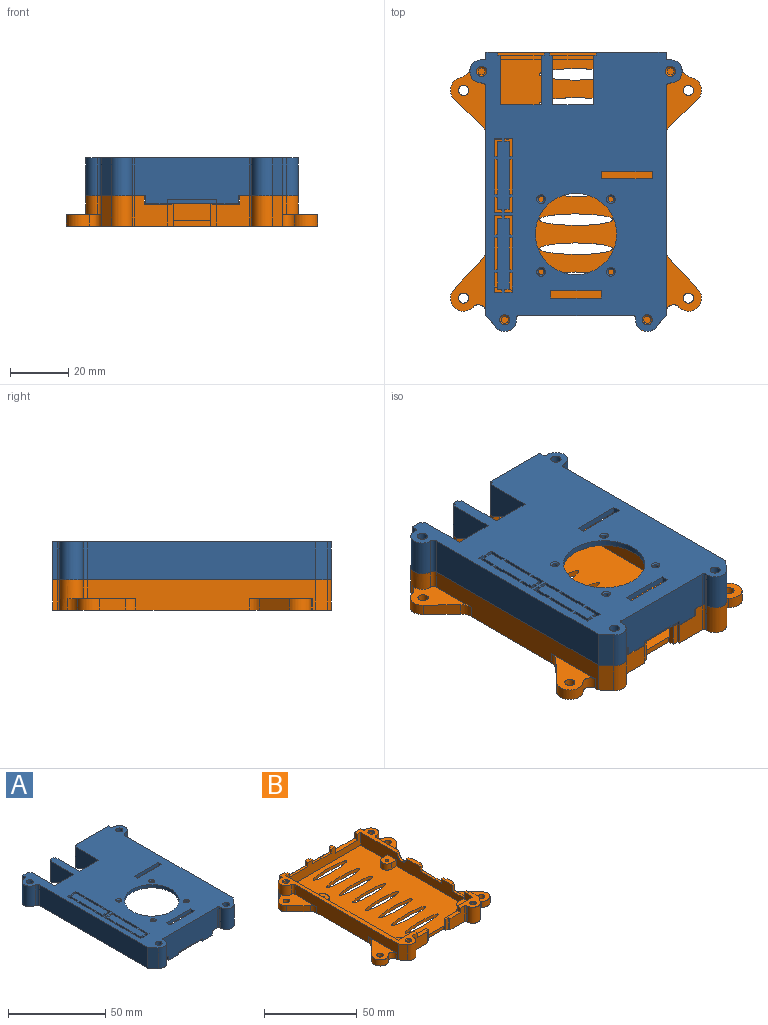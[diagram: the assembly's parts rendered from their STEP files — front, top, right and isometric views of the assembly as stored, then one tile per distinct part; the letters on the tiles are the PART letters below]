
ASSEMBLY  parts=2 mates=1
PART A: 159 faces, bbox 73x96x15.8 mm
  f0: plane 32x2.5mm, normal (0,0,-1), area 63mm2, adj f67,f68,f153,f154,f155,f156,f157
  f1: plane 96x20.5mm, normal (0,0,-1), area 322.4mm2, adj f67,f68,f69,f70,f71,f72,f73,f74
  f2: plane 30.5x10.5mm, normal (0,0,-1), area 109.1mm2, adj f3,f4,f65,f90,f91,f92,f93,f94
  f3: plane 78.5x13mm, normal (1,0,0), area 841.2mm2, adj f2,f5,f6,f52,f85,f89,f90,f140
  f4: plane 85.5x11mm, normal (-1,0,0), area 848.3mm2, adj f2,f5,f6,f7,f68,f85,f96,f136
  f5: plane 10.5x2.5mm, normal (0,0,-1), area 22.8mm2, adj f3,f4,f144,f146,f147,f150,f151,f152
  f6: plane 8.5x2.5mm, normal (0,0,-1), area 17.8mm2, adj f3,f4,f137,f139,f140,f143,f146,f148
  f7: plane 85.5x57mm, normal (0,0,-1), area 2695.7mm2, adj f4,f53,f59,f63,f64,f68,f69,f70
  f8: plane 12x1.2mm, normal (1,0,0), area 14.4mm2, adj f9,f10,f52,f134
  f9: plane 1.2x1mm, normal (0,-1,0), area 1.2mm2, adj f8,f52,f125,f134
  f10: plane 1.2x1mm, normal (0,1,0), area 1.2mm2, adj f8,f52,f125,f134
  f11: plane 1.2x1mm, normal (0,-1,0), area 1.2mm2, adj f13,f52,f123,f134
  f12: plane 1.2x1mm, normal (0,1,0), area 1.2mm2, adj f13,f52,f123,f134
  f13: plane 12x1.2mm, normal (-1,0,0), area 14.4mm2, adj f11,f12,f52,f134
  f14: plane 1.2x1mm, normal (-1,0,0), area 1.2mm2, adj f16,f52,f106,f134
  f15: plane 1.2x1mm, normal (0,-1,0), area 1.2mm2, adj f17,f52,f123,f134
  f16: plane 1.5x1.2mm, normal (0,-1,0), area 1.8mm2, adj f14,f17,f52,f134
  f17: plane 4.25x1.2mm, normal (-1,0,0), area 5.1mm2, adj f15,f16,f52,f134
  f18: plane 1.2x1mm, normal (0,-1,0), area 1.2mm2, adj f20,f52,f125,f134
  f19: plane 1.2x1mm, normal (1,0,0), area 1.2mm2, adj f21,f52,f106,f134
  f20: plane 4.25x1.2mm, normal (1,0,0), area 5.1mm2, adj f18,f21,f52,f134
  f21: plane 1.5x1.2mm, normal (0,-1,0), area 1.8mm2, adj f19,f20,f52,f134
  f22: plane 1.2x1mm, normal (1,0,0), area 1.2mm2, adj f23,f52,f107,f135
  f23: plane 1.5x1.2mm, normal (0,1,0), area 1.8mm2, adj f22,f24,f52,f135
  f24: plane 5.75x1.2mm, normal (1,0,0), area 6.9mm2, adj f23,f25,f52,f135
  f25: plane 1.2x1mm, normal (0,1,0), area 1.2mm2, adj f24,f52,f122,f135
  f26: plane 1.2x1mm, normal (0,1,0), area 1.2mm2, adj f27,f52,f120,f135
  f27: plane 5.75x1.2mm, normal (-1,0,0), area 6.9mm2, adj f26,f28,f52,f135
  f28: plane 1.5x1.2mm, normal (0,1,0), area 1.8mm2, adj f27,f29,f52,f135
  f29: plane 1.2x1mm, normal (-1,0,0), area 1.2mm2, adj f28,f52,f107,f135
  f30: plane 1.2x1mm, normal (0,-1,0), area 1.2mm2, adj f32,f52,f120,f135
  f31: plane 1.2x1mm, normal (0,1,0), area 1.2mm2, adj f32,f52,f120,f135
  f32: plane 11x1.2mm, normal (-1,0,0), area 13.2mm2, adj f30,f31,f52,f135
  f33: plane 1.2x1mm, normal (0,-1,0), area 1.2mm2, adj f34,f52,f122,f135
  f34: plane 11x1.2mm, normal (1,0,0), area 13.2mm2, adj f33,f35,f52,f135
  f35: plane 1.2x1mm, normal (0,1,0), area 1.2mm2, adj f34,f52,f122,f135
  f36: plane 1.2x1mm, normal (-1,0,0), area 1.2mm2, adj f37,f52,f121,f135
  f37: plane 1.5x1.2mm, normal (0,-1,0), area 1.8mm2, adj f36,f38,f52,f135
  f38: plane 5.75x1.2mm, normal (-1,0,0), area 6.9mm2, adj f37,f39,f52,f135
  f39: plane 1.2x1mm, normal (0,-1,0), area 1.2mm2, adj f38,f52,f120,f135
  f40: plane 1.2x1mm, normal (0,-1,0), area 1.2mm2, adj f42,f52,f122,f135
  f41: plane 1.2x1mm, normal (1,0,0), area 1.2mm2, adj f43,f52,f121,f135
  f42: plane 5.75x1.2mm, normal (1,0,0), area 6.9mm2, adj f40,f43,f52,f135
  f43: plane 1.5x1.2mm, normal (0,-1,0), area 1.8mm2, adj f41,f42,f52,f135
  f44: plane 1.2x1mm, normal (0,1,0), area 1.2mm2, adj f45,f52,f123,f134
  f45: plane 5.25x1.2mm, normal (-1,0,0), area 6.3mm2, adj f44,f46,f52,f134
  f46: plane 1.5x1.2mm, normal (0,1,0), area 1.8mm2, adj f45,f47,f52,f134
  f47: plane 1.2x1mm, normal (-1,0,0), area 1.2mm2, adj f46,f52,f124,f134
  f48: plane 1.2x1mm, normal (1,0,0), area 1.2mm2, adj f49,f52,f124,f134
  f49: plane 1.5x1.2mm, normal (0,1,0), area 1.8mm2, adj f48,f50,f52,f134
  f50: plane 5.25x1.2mm, normal (1,0,0), area 6.3mm2, adj f49,f51,f52,f134
  f51: plane 1.2x1mm, normal (0,1,0), area 1.2mm2, adj f50,f52,f125,f134
  f52: plane 96x73mm, normal (0,0,1), area 4382.9mm2, adj f3,f8,f9,f10,f11,f12,f13,f14
  f53: plane 32x13mm, normal (1,0,0), area 186.2mm2, adj f7,f52,f54,f60,f97,f99,f103,f104
  f54: plane 13x1mm, normal (0,1,0), area 13mm2, adj f52,f53,f55,f60
  f55: plane 13x1mm, normal (1,0,0), area 13mm2, adj f52,f54,f56,f60
  f56: plane 13x2mm, normal (0,1,0), area 26mm2, adj f52,f55,f57,f60
  f57: plane 13x1mm, normal (-1,0,0), area 13mm2, adj f52,f56,f58,f60
  f58: plane 13x1mm, normal (0,1,0), area 13mm2, adj f52,f57,f59,f60
  f59: plane 24x13mm, normal (-1,0,0), area 174.3mm2, adj f7,f52,f58,f60,f98,f99
  f60: plane 4x2.5mm, normal (0,0,-1), area 8mm2, adj f53,f54,f55,f56,f57,f58,f59,f99
  f61: plane 13x1mm, normal (-1,0,0), area 13mm2, adj f52,f62,f65,f66
  f62: plane 13x1mm, normal (0,1,0), area 13mm2, adj f52,f61,f63,f66
  f63: plane 32x13mm, normal (-1,0,0), area 186.3mm2, adj f7,f52,f62,f66,f97,f100,f103,f104
  f64: plane 25x11.8mm, normal (1,0,0), area 169.6mm2, adj f7,f65,f66,f100,f101,f102
  f65: plane 24x13mm, normal (0,1,0), area 111.4mm2, adj f2,f52,f61,f64,f66,f94,f95,f102
  f66: plane 3x2.5mm, normal (0,0,-1), area 6.5mm2, adj f61,f62,f63,f64,f65,f100
  f67: plane 39.5x15.8mm, normal (0,-1,0), area 577.6mm2, adj f0,f1,f52,f84,f85,f86,f153,f154
  f68: plane 57x13.8mm, normal (0,1,0), area 716.6mm2, adj f0,f1,f4,f7,f69,f85,f153,f154
  f69: plane 85.5x11mm, normal (1,0,0), area 940.5mm2, adj f1,f7,f68,f70
  f70: plane 11x2.5mm, normal (0,-1,0), area 27.5mm2, adj f1,f7,f69,f71
  f71: plane 17x13mm, normal (1,0,0), area 50.5mm2, adj f1,f7,f52,f70,f72,f98
  f72: plane 13x1mm, normal (0,1,0), area 13mm2, adj f1,f52,f71,f73
  f73: plane 13x1mm, normal (1,0,0), area 13mm2, adj f1,f52,f72,f74
  f74: plane 13x4mm, normal (0,1,0), area 52mm2, adj f1,f52,f73,f75
  f75: plane 13x1.75mm, normal (-1,0,0), area 22.8mm2, adj f1,f52,f74,f76
  f76: cylinder r=0.75mm len=13mm, axis (0,0,-1), area 15.3mm2, adj f1,f52,f75,f77
  f77: plane 13x0.75mm, normal (0,1,0), area 9.7mm2, adj f1,f52,f76,f78
  f78: cylinder r=4mm len=13mm, axis (0,0,-1), area 163.4mm2, adj f1,f52,f77,f79
  f79: cylinder r=1.5mm len=13mm, axis (0,0,-1), area 30.6mm2, adj f1,f52,f78,f80
  f80: plane 78.5x13mm, normal (-1,0,0), area 1020.5mm2, adj f1,f52,f79,f81
  f81: plane 13x4.08mm, normal (-0.76,-0.64,0), area 69.4mm2, adj f1,f52,f80,f82
  f82: cylinder r=4mm len=13mm, axis (0,0,-1), area 126.9mm2, adj f1,f52,f81,f83
  f83: plane 13x0.75mm, normal (1,0,0), area 9.7mm2, adj f1,f52,f82,f84
  f84: cylinder r=0.75mm len=13mm, axis (0,0,-1), area 15.3mm2, adj f1,f52,f67,f83
  f85: plane 15x14.5mm, normal (0,0,-1), area 83.8mm2, adj f3,f4,f67,f68,f86,f87,f88,f89
  f86: cylinder r=0.75mm len=13mm, axis (0,0,-1), area 15.3mm2, adj f52,f67,f85,f87
  f87: plane 13x0.75mm, normal (-1,0,0), area 9.7mm2, adj f52,f85,f86,f88
  f88: cylinder r=4mm len=13mm, axis (0,0,-1), area 126.9mm2, adj f52,f85,f87,f89
  f89: plane 13x4.08mm, normal (0.76,-0.64,0), area 69.4mm2, adj f3,f52,f85,f88
  f90: cylinder r=1.5mm len=13mm, axis (0,0,-1), area 30.6mm2, adj f2,f3,f52,f91
  f91: cylinder r=4mm len=13mm, axis (0,0,-1), area 163.4mm2, adj f2,f52,f90,f92
  f92: plane 13x0.75mm, normal (0,1,0), area 9.8mm2, adj f2,f52,f91,f93
  f93: cylinder r=0.75mm len=13mm, axis (0,0,-1), area 15.3mm2, adj f2,f52,f92,f94
  f94: plane 13x1.75mm, normal (1,0,0), area 22.8mm2, adj f2,f52,f65,f93
  f95: plane 23x11.8mm, normal (-1,0,0), area 45.9mm2, adj f2,f7,f65,f96,f101,f102
  f96: plane 11x2.5mm, normal (0,-1,0), area 27.5mm2, adj f2,f4,f7,f95
  f97: plane 14x1.2mm, normal (0,1,0), area 16.8mm2, adj f52,f53,f63,f104
  f98: plane 14x2mm, normal (0,1,0), area 28mm2, adj f7,f52,f59,f71
  f99: plane 22.5x11mm, normal (0,-0.44,-0.9), area 100.2mm2, adj f7,f53,f59,f60
  f100: plane 22.5x11mm, normal (0,-0.44,-0.9), area 75.1mm2, adj f7,f63,f64,f66
  f101: plane 17x0.8mm, normal (0,1,0), area 13.6mm2, adj f7,f64,f95,f102
  f102: plane 23x17mm, normal (0,0,-1), area 391mm2, adj f64,f65,f95,f101
  f103: plane 14x0.8mm, normal (0,1,0), area 11.2mm2, adj f7,f53,f63,f104
  f104: plane 15x14mm, normal (0,0,-1), area 210mm2, adj f53,f63,f97,f103
  f105: cylinder r=14mm len=28mm, axis (0,0,1), area 175.9mm2, adj f7,f52
  f106: plane 6x2mm, normal (0,1,0), area 10.8mm2, adj f7,f14,f19,f52,f123,f125,f134
  f107: plane 6x2mm, normal (0,-1,0), area 10.8mm2, adj f7,f22,f29,f52,f120,f122,f135
  f108: cylinder r=1mm len=2mm, axis (0,0,1), area 9.4mm2, adj f7,f127
  f109: plane 2.5x2mm, normal (1,0,0), area 5mm2, adj f7,f52,f110,f111
  f110: plane 17.5x2mm, normal (0,-1,0), area 35mm2, adj f7,f52,f109,f112
  f111: plane 17.5x2mm, normal (0,1,0), area 35mm2, adj f7,f52,f109,f112
  f112: plane 2.5x2mm, normal (-1,0,0), area 5mm2, adj f7,f52,f110,f111
  f113: cylinder r=1mm len=2mm, axis (0,0,1), area 9.4mm2, adj f7,f126
  f114: cylinder r=1mm len=2mm, axis (0,0,1), area 9.4mm2, adj f7,f129
  f115: cylinder r=1mm len=2mm, axis (0,0,1), area 9.4mm2, adj f7,f128
  f116: plane 2.5x2mm, normal (1,0,0), area 5mm2, adj f7,f52,f117,f118
  f117: plane 17.5x2mm, normal (0,-1,0), area 35mm2, adj f7,f52,f116,f119
  f118: plane 17.5x2mm, normal (0,1,0), area 35mm2, adj f7,f52,f116,f119
  f119: plane 2.5x2mm, normal (-1,0,0), area 5mm2, adj f7,f52,f117,f118
  f120: plane 26.5x2mm, normal (1,0,0), area 50.6mm2, adj f7,f26,f30,f31,f39,f52,f107,f121
  f121: plane 6x2mm, normal (0,1,0), area 10.8mm2, adj f7,f36,f41,f52,f120,f122,f135
  f122: plane 26.5x2mm, normal (-1,0,0), area 50.6mm2, adj f7,f25,f33,f35,f40,f52,f107,f121
  f123: plane 25.5x2mm, normal (1,0,0), area 48.6mm2, adj f7,f11,f12,f15,f44,f52,f106,f124
  f124: plane 6x2mm, normal (0,-1,0), area 10.8mm2, adj f7,f47,f48,f52,f123,f125,f134
  f125: plane 25.5x2mm, normal (-1,0,0), area 48.6mm2, adj f7,f9,f10,f18,f51,f52,f106,f124
  f126: cone r=1mm half-angle=45deg, axis (0,0,1), area 5.6mm2, adj f52,f113
  f127: cone r=1mm half-angle=45deg, axis (0,0,1), area 5.6mm2, adj f52,f108
  f128: cone r=1mm half-angle=45deg, axis (0,0,1), area 5.6mm2, adj f52,f115
  f129: cone r=1mm half-angle=45deg, axis (0,0,1), area 5.6mm2, adj f52,f114
  f130: cylinder r=1.75mm len=13mm, axis (0,0,1), area 142.9mm2, adj f1,f52
  f131: cylinder r=1.75mm len=13mm, axis (0,0,1), area 142.9mm2, adj f52,f85
  f132: cylinder r=1.75mm len=13mm, axis (0,0,1), area 142.9mm2, adj f2,f52
  f133: cylinder r=1.75mm len=13mm, axis (0,0,1), area 142.9mm2, adj f1,f52
  f134: plane 25.5x6mm, normal (0,0,-1), area 100mm2, adj f8,f9,f10,f11,f12,f13,f14,f15
  f135: plane 26.5x6mm, normal (0,0,-1), area 104mm2, adj f22,f23,f24,f25,f26,f27,f28,f29
  f136: plane 1.5x1mm, normal (0,1,0), area 1.5mm2, adj f4,f85,f138,f139
  f137: plane 1.5x1mm, normal (0,-1,0), area 1.5mm2, adj f4,f6,f138,f139
  f138: plane 9x1.5mm, normal (0,0,-1), area 13.5mm2, adj f4,f136,f137,f139
  f139: plane 12x2.5mm, normal (1,0,0), area 21mm2, adj f6,f85,f136,f137,f138,f140,f141,f142
  f140: plane 2.5x1mm, normal (0,-1,0), area 2.5mm2, adj f3,f6,f139,f142
  f141: plane 2.5x1mm, normal (0,1,0), area 2.5mm2, adj f3,f85,f139,f142
  f142: plane 12x1mm, normal (0,0,-1), area 12mm2, adj f3,f139,f140,f141
  f143: plane 4x1.5mm, normal (0,1,0), area 6mm2, adj f4,f6,f145,f146
  f144: plane 4x1.5mm, normal (0,-1,0), area 6mm2, adj f4,f5,f145,f146
  f145: plane 16x1.5mm, normal (0,0,-1), area 24mm2, adj f4,f143,f144,f146
  f146: plane 20x5.5mm, normal (1,0,0), area 46mm2, adj f5,f6,f143,f144,f145,f147,f148,f149
  f147: plane 5.5x1mm, normal (0,-1,0), area 5.5mm2, adj f3,f5,f146,f149
  f148: plane 5.5x1mm, normal (0,1,0), area 5.5mm2, adj f3,f6,f146,f149
  f149: plane 20x1mm, normal (0,0,-1), area 20mm2, adj f3,f146,f147,f148
  f150: cylinder r=3.5mm len=7mm, axis (1,0,0), area 16.5mm2, adj f2,f4,f5,f152
  f151: cylinder r=5mm len=10mm, axis (1,0,0), area 15.7mm2, adj f2,f3,f5,f152
  f152: plane 10x5mm, normal (1,0,0), area 20mm2, adj f2,f5,f150,f151
  f153: plane 2.8x2.5mm, normal (-1,0,0), area 7mm2, adj f0,f1,f67,f68
  f154: plane 2.8x2.5mm, normal (1,0,0), area 7mm2, adj f0,f67,f68,f85
  f155: plane 1.5x1mm, normal (1,0,0), area 1.5mm2, adj f0,f67,f156,f158
  f156: plane 17x1.5mm, normal (0,-1,0), area 25.5mm2, adj f0,f155,f157,f158
  f157: plane 1.5x1mm, normal (-1,0,0), area 1.5mm2, adj f0,f67,f156,f158
  f158: plane 17x1mm, normal (0,0,-1), area 17mm2, adj f67,f155,f156,f157
PART B: 150 faces, bbox 86.4x96x10.5 mm
  f0: cylinder r=1.25mm len=7mm, axis (0,0,-1), area 55mm2, adj f145,f146
  f1: cylinder r=1.25mm len=7mm, axis (0,0,-1), area 55mm2, adj f144,f147
  f2: cylinder r=1.25mm len=7mm, axis (0,0,-1), area 55mm2, adj f143,f148
  f3: cylinder r=1.25mm len=7mm, axis (0,0,-1), area 55mm2, adj f142,f149
  f4: plane 78.5x10.5mm, normal (1,0,0), area 466.2mm2, adj f10,f11,f21,f22,f23,f68,f69,f70
  f5: plane 78.5x10.5mm, normal (-1,0,0), area 671.5mm2, adj f10,f14,f97,f105,f117,f121,f122,f125
  f6: plane 11.25x10.5mm, normal (0,-1,0), area 94.1mm2, adj f10,f11,f88,f89,f92,f99
  f7: plane 11.25x10.5mm, normal (0,-1,0), area 94.1mm2, adj f10,f14,f86,f87,f91,f94
  f8: plane 7.5x2mm, normal (-1,0,0), area 12.2mm2, adj f10,f33,f35,f39,f88,f93
  f9: plane 7.5x2mm, normal (1,0,0), area 12.2mm2, adj f10,f12,f35,f39,f86,f90
  f10: plane 96x86.39mm, normal (0,0,-1), area 5621.8mm2, adj f4,f5,f6,f7,f8,f9,f24,f35
  f11: plane 14.5x14.5mm, normal (0,0,1), area 82.6mm2, adj f4,f6,f28,f32,f33,f68,f71,f89
  f12: plane 22x8.5mm, normal (0,1,0), area 127mm2, adj f9,f14,f34,f39,f47,f50,f86,f87
  f13: plane 4x2.5mm, normal (0,0,1), area 8mm2, adj f15,f20,f36,f38,f80,f81,f82,f85
  f14: plane 96x20mm, normal (0,0,1), area 321.2mm2, adj f5,f7,f12,f17,f34,f36,f37,f38
  f15: plane 2.5x1.5mm, normal (-1,0,0), area 3.8mm2, adj f13,f16,f38,f85
  f16: plane 14x1.5mm, normal (0,0,1), area 21mm2, adj f15,f17,f38,f85
  f17: plane 2.5x1.5mm, normal (1,0,0), area 3.8mm2, adj f14,f16,f38,f85
  f18: plane 2.5x1.5mm, normal (-1,0,0), area 3.8mm2, adj f19,f31,f38,f81
  f19: plane 14x1.5mm, normal (0,0,1), area 21mm2, adj f18,f20,f38,f81
  f20: plane 2.5x1.5mm, normal (1,0,0), area 3.8mm2, adj f13,f19,f38,f81
  f21: plane 8.5x2.5mm, normal (0,0,1), area 17.8mm2, adj f4,f25,f30,f32,f70,f71,f72,f75
  f22: plane 10.5x2.5mm, normal (0,0,1), area 22.8mm2, adj f4,f27,f32,f64,f74,f75,f76,f77
  f23: plane 30.5x10.5mm, normal (0,0,1), area 109.1mm2, adj f4,f24,f32,f36,f38,f64,f65,f76
  f24: plane 10.5x1.75mm, normal (1,0,0), area 18.4mm2, adj f10,f23,f36,f108
  f25: plane 3x1.5mm, normal (0,1,0), area 4.5mm2, adj f21,f26,f32,f75
  f26: plane 16x1.5mm, normal (0,0,1), area 24mm2, adj f25,f27,f32,f75
  f27: plane 3x1.5mm, normal (0,-1,0), area 4.5mm2, adj f22,f26,f32,f75
  f28: plane 4x1.5mm, normal (0,1,0), area 6mm2, adj f11,f29,f32,f71
  f29: plane 9x1.5mm, normal (0,0,1), area 13.5mm2, adj f28,f30,f32,f71
  f30: plane 4x1.5mm, normal (0,-1,0), area 6mm2, adj f21,f29,f32,f71
  f31: plane 3x2.5mm, normal (0,0,1), area 6.5mm2, adj f18,f36,f38,f67,f78,f81
  f32: plane 85.5x8.5mm, normal (-1,0,0), area 567.5mm2, adj f11,f21,f22,f23,f25,f26,f27,f28
  f33: plane 22x8.5mm, normal (0,1,0), area 127mm2, adj f8,f11,f32,f39,f54,f56,f88,f89
  f34: plane 85.5x8.5mm, normal (1,0,0), area 670.8mm2, adj f12,f14,f38,f39,f40,f43,f44,f46
  f35: plane 13x2mm, normal (0,-1,0), area 26mm2, adj f8,f9,f10,f39
  f36: plane 62x10.5mm, normal (0,1,0), area 471mm2, adj f10,f13,f14,f23,f24,f31,f37,f65
  f37: plane 10.5x1.75mm, normal (-1,0,0), area 18.4mm2, adj f10,f14,f36,f104
  f38: plane 57x8.5mm, normal (0,-1,0), area 346.5mm2, adj f13,f14,f15,f16,f17,f18,f19,f20
  f39: plane 85.5x57mm, normal (0,0,1), area 4044.5mm2, adj f8,f9,f12,f32,f33,f34,f35,f38
  f40: plane 4x4mm, normal (0,-1,0), area 16mm2, adj f34,f39,f41,f44
  f41: cylinder r=3.5mm len=7mm, axis (0,0,-1), area 44mm2, adj f39,f40,f43,f44
  f42: cylinder r=1mm len=4mm, axis (0,0,-1), area 25.1mm2, adj f44,f45
  f43: plane 4x4mm, normal (0,1,0), area 16mm2, adj f34,f39,f41,f44
  f44: plane 7.5x7mm, normal (0,0,1), area 44.1mm2, adj f34,f40,f41,f42,f43
  f45: plane 2x2mm, normal (0,0,1), area 3.1mm2, adj f42
  f46: plane 4x4mm, normal (0,1,0), area 16mm2, adj f34,f39,f48,f50
  f47: plane 4x3.5mm, normal (1,0,0), area 14mm2, adj f12,f39,f48,f50
  f48: cylinder r=3.5mm len=4mm, axis (0,0,-1), area 22mm2, adj f39,f46,f47,f50
  f49: cylinder r=1mm len=4mm, axis (0,0,-1), area 25.1mm2, adj f50,f51
  f50: plane 7.5x7mm, normal (0,0,1), area 46.7mm2, adj f12,f34,f46,f47,f48,f49
  f51: plane 2x2mm, normal (0,0,1), area 3.1mm2, adj f49
  f52: plane 4x4mm, normal (0,1,0), area 16mm2, adj f32,f39,f53,f56
  f53: cylinder r=3.5mm len=4mm, axis (0,0,-1), area 22mm2, adj f39,f52,f54,f56
  f54: plane 4x3.5mm, normal (-1,0,0), area 14mm2, adj f33,f39,f53,f56
  f55: cylinder r=1mm len=4mm, axis (0,0,-1), area 25.1mm2, adj f56,f57
  f56: plane 7.5x7mm, normal (0,0,1), area 46.7mm2, adj f32,f33,f52,f53,f54,f55
  f57: plane 2x2mm, normal (0,0,1), area 3.1mm2, adj f55
  f58: plane 4x4mm, normal (0,1,0), area 16mm2, adj f32,f39,f59,f62
  f59: cylinder r=3.5mm len=7mm, axis (0,0,-1), area 44mm2, adj f39,f58,f61,f62
  f60: cylinder r=1mm len=4mm, axis (0,0,-1), area 25.1mm2, adj f62,f63
  f61: plane 4x4mm, normal (0,-1,0), area 16mm2, adj f32,f39,f59,f62
  f62: plane 7.5x7mm, normal (0,0,1), area 44.1mm2, adj f32,f58,f59,f60,f61
  f63: plane 2x2mm, normal (0,0,1), area 3.1mm2, adj f60
  f64: cylinder r=3.5mm len=7mm, axis (1,0,0), area 16.5mm2, adj f22,f23,f32,f77
  f65: plane 4x2.5mm, normal (-1,0,0), area 10mm2, adj f23,f36,f38,f66
  f66: plane 17x2.5mm, normal (0,0,1), area 42.5mm2, adj f36,f38,f65,f67
  f67: plane 4x2.5mm, normal (1,0,0), area 10mm2, adj f31,f36,f38,f66
  f68: plane 5.5x1mm, normal (0,1,0), area 5.5mm2, adj f4,f11,f69,f71
  f69: plane 12x1mm, normal (0,0,1), area 12mm2, adj f4,f68,f70,f71
  f70: plane 5.5x1mm, normal (0,-1,0), area 5.5mm2, adj f4,f21,f69,f71
  f71: plane 12x5.5mm, normal (1,0,0), area 30mm2, adj f11,f21,f28,f29,f30,f68,f69,f70
  f72: plane 5x1mm, normal (0,1,0), area 5mm2, adj f4,f21,f73,f75
  f73: plane 20x1mm, normal (0,0,1), area 20mm2, adj f4,f72,f74,f75
  f74: plane 5x1mm, normal (0,-1,0), area 5mm2, adj f4,f22,f73,f75
  f75: plane 20x5mm, normal (1,0,0), area 52mm2, adj f21,f22,f25,f26,f27,f72,f73,f74
  f76: cylinder r=5mm len=10mm, axis (1,0,0), area 15.7mm2, adj f4,f22,f23,f77
  f77: plane 10x5mm, normal (1,0,0), area 20mm2, adj f22,f23,f64,f76
  f78: plane 3.5x1mm, normal (-1,0,0), area 3.5mm2, adj f31,f36,f79,f81
  f79: plane 16x1mm, normal (0,0,1), area 16mm2, adj f36,f78,f80,f81
  f80: plane 3.5x1mm, normal (1,0,0), area 3.5mm2, adj f13,f36,f79,f81
  f81: plane 16x3.5mm, normal (0,1,0), area 21mm2, adj f13,f18,f19,f20,f31,f78,f79,f80
  f82: plane 3.5x1mm, normal (-1,0,0), area 3.5mm2, adj f13,f36,f83,f85
  f83: plane 16x1mm, normal (0,0,1), area 16mm2, adj f36,f82,f84,f85
  f84: plane 3.5x1mm, normal (1,0,0), area 3.5mm2, adj f14,f36,f83,f85
  f85: plane 16x3.5mm, normal (0,1,0), area 21mm2, adj f13,f14,f15,f16,f17,f82,f83,f84
  f86: plane 10x2.5mm, normal (0,0,1), area 23mm2, adj f7,f9,f12,f87,f90,f91
  f87: plane 3x2.5mm, normal (1,0,0), area 7.5mm2, adj f7,f12,f14,f86
  f88: plane 10x2.5mm, normal (0,0,1), area 23mm2, adj f6,f8,f33,f89,f92,f93
  f89: plane 3x2.5mm, normal (-1,0,0), area 7.5mm2, adj f6,f11,f33,f88
  f90: plane 7.5x2mm, normal (0,-1,0), area 15mm2, adj f9,f10,f86,f91
  f91: plane 7.5x1mm, normal (1,0,0), area 7.5mm2, adj f7,f10,f86,f90
  f92: plane 7.5x1mm, normal (-1,0,0), area 7.5mm2, adj f6,f10,f88,f93
  f93: plane 7.5x2mm, normal (0,-1,0), area 15mm2, adj f8,f10,f88,f92
  f94: cylinder r=0.75mm len=10.5mm, axis (0,0,-1), area 12.4mm2, adj f7,f10,f14,f95
  f95: plane 10.5x0.75mm, normal (1,0,0), area 7.9mm2, adj f10,f14,f94,f96
  f96: cylinder r=4mm len=10.5mm, axis (0,0,-1), area 102.5mm2, adj f10,f14,f95,f97
  f97: plane 10.5x4.08mm, normal (-0.76,-0.64,0), area 56.1mm2, adj f5,f10,f14,f96
  f98: plane 10.5x0.75mm, normal (-1,0,0), area 7.9mm2, adj f10,f11,f99,f101
  f99: cylinder r=0.75mm len=10.5mm, axis (0,0,-1), area 12.4mm2, adj f6,f10,f11,f98
  f100: plane 10.5x4.08mm, normal (0.76,-0.64,0), area 56.1mm2, adj f4,f10,f11,f101
  f101: cylinder r=4mm len=10.5mm, axis (0,0,-1), area 102.5mm2, adj f10,f11,f98,f100
  f102: cylinder r=4mm len=10.5mm, axis (0,0,-1), area 102mm2, adj f10,f14,f103,f105,f116,f121
  f103: plane 10.5x0.75mm, normal (0,1,0), area 7.9mm2, adj f10,f14,f102,f104
  f104: cylinder r=0.75mm len=10.5mm, axis (0,0,-1), area 12.4mm2, adj f10,f14,f37,f103
  f105: cylinder r=1.5mm len=6.5mm, axis (0,0,-1), area 15.3mm2, adj f5,f14,f102,f121
  f106: cylinder r=4mm len=10.5mm, axis (0,0,-1), area 102mm2, adj f10,f23,f107,f109,f110,f115
  f107: cylinder r=1.5mm len=6.5mm, axis (0,0,-1), area 15.3mm2, adj f4,f23,f106,f115
  f108: cylinder r=0.75mm len=10.5mm, axis (0,0,-1), area 12.4mm2, adj f10,f23,f24,f109
  f109: plane 10.5x0.75mm, normal (0,1,0), area 7.9mm2, adj f10,f23,f106,f108
  f110: cylinder r=5mm len=4mm, axis (0,0,-1), area 20.3mm2, adj f10,f106,f111,f115
  f111: cylinder r=4.5mm len=7.62mm, axis (0,0,-1), area 38.3mm2, adj f10,f110,f112,f115
  f112: plane 9.24x8.76mm, normal (0.69,-0.73,0), area 50.9mm2, adj f10,f111,f113,f115
  f113: cylinder r=5mm len=4mm, axis (0,0,-1), area 16.2mm2, adj f4,f10,f112,f115
  f114: cylinder r=1.75mm len=4mm, axis (0,0,-1), area 44mm2, adj f10,f115
  f115: plane 23.37x12.2mm, normal (0,0,1), area 130.1mm2, adj f4,f106,f107,f110,f111,f112,f113,f114
  f116: cylinder r=5mm len=4mm, axis (0,0,-1), area 20.3mm2, adj f10,f102,f120,f121
  f117: cylinder r=5mm len=4mm, axis (0,0,-1), area 16.2mm2, adj f5,f10,f118,f121
  f118: plane 9.24x8.76mm, normal (-0.69,-0.73,0), area 50.9mm2, adj f10,f117,f120,f121
  f119: cylinder r=1.75mm len=4mm, axis (0,0,-1), area 44mm2, adj f10,f121
  f120: cylinder r=4.5mm len=7.62mm, axis (0,0,-1), area 38.3mm2, adj f10,f116,f118,f121
  f121: plane 23.37x12.2mm, normal (0,0,1), area 130.1mm2, adj f5,f102,f105,f116,f117,f118,f119,f120
  f122: cylinder r=2.57mm len=4.43mm, axis (0,0,-1), area 24.5mm2, adj f5,f10,f123,f127
  f123: cylinder r=4.5mm len=7.76mm, axis (0,0,-1), area 56.5mm2, adj f10,f122,f124,f127
  f124: plane 10.1x9.59mm, normal (-0.73,0.69,0), area 55.7mm2, adj f10,f123,f125,f127
  f125: cylinder r=5mm len=4mm, axis (0,0,-1), area 15.2mm2, adj f5,f10,f124,f127
  f126: cylinder r=1.75mm len=4mm, axis (0,0,-1), area 44mm2, adj f10,f127
  f127: plane 21.51x12.2mm, normal (0,0,1), area 132mm2, adj f5,f122,f123,f124,f125,f126
  f128: plane 10.1x9.59mm, normal (0.73,0.69,0), area 55.7mm2, adj f10,f129,f131,f133
  f129: cylinder r=4.5mm len=7.76mm, axis (0,0,-1), area 56.5mm2, adj f10,f128,f130,f133
  f130: cylinder r=2.57mm len=4.43mm, axis (0,0,-1), area 24.5mm2, adj f4,f10,f129,f133
  f131: cylinder r=5mm len=4mm, axis (0,0,-1), area 15.2mm2, adj f4,f10,f128,f133
  f132: cylinder r=1.75mm len=4mm, axis (0,0,-1), area 44mm2, adj f10,f133
  f133: plane 21.51x12.2mm, normal (0,0,1), area 132mm2, adj f4,f128,f129,f130,f131,f132
  f134: extruded ~25x4mm, area 103.7mm2, adj f10,f39
  f135: extruded ~25x4mm, area 103.7mm2, adj f10,f39
  f136: extruded ~25x4mm, area 103.7mm2, adj f10,f39
  f137: extruded ~25x4mm, area 103.7mm2, adj f10,f39
  f138: extruded ~25x4mm, area 103.7mm2, adj f10,f39
  f139: extruded ~25x4mm, area 103.7mm2, adj f10,f39
  f140: extruded ~25x4mm, area 103.7mm2, adj f10,f39
  f141: extruded ~25x4mm, area 103.7mm2, adj f10,f39
  f142: plane 2.5x2.5mm, normal (0,0,1), area 4.9mm2, adj f3
  f143: plane 2.5x2.5mm, normal (0,0,1), area 4.9mm2, adj f2
  f144: plane 2.5x2.5mm, normal (0,0,1), area 4.9mm2, adj f1
  f145: plane 2.5x2.5mm, normal (0,0,1), area 4.9mm2, adj f0
  f146: cone r=1.75mm half-angle=45deg, axis (0,0,1), area 6.7mm2, adj f0,f23
  f147: cone r=1.75mm half-angle=45deg, axis (0,0,1), area 6.7mm2, adj f1,f14
  f148: cone r=1.75mm half-angle=45deg, axis (0,0,1), area 6.7mm2, adj f2,f11
  f149: cone r=1.75mm half-angle=45deg, axis (0,0,1), area 6.7mm2, adj f3,f14
PLACE A t=(-37.02,-28.16,-75.15)mm
PLACE B t=(-37.02,-28.16,24.85)mm
MATE fastened A.f88 <-> B.f2  axis (0,0,-1) through (18.48,-29.66,35.35)mm
